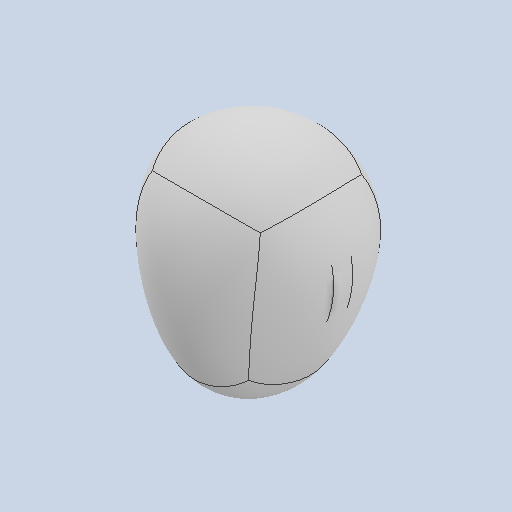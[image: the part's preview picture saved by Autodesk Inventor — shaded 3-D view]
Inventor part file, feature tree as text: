
AUTODESK INVENTOR PART (.ipt)
format: ipt  version: 2025 (Build 290162010, 162A)  size: 317,952 bytes
history: native  units: mm
features: other x2, extrude x2, sketch x1
ambient origin geometry x8: Origin, YZ Plane, XZ Plane, XY Plane, X Axis, Y Axis, Z Axis, Center Point
bodies: Solid3 (feature_tree)
feature tree (5):
  other  "Твердое тело1"
  extrude  "Выдавливание1"  Depth=180.0mm
  other  "Form2"
  extrude  "Extrusion2"  Depth=120.0mm
  sketch  "Эскиз1"
